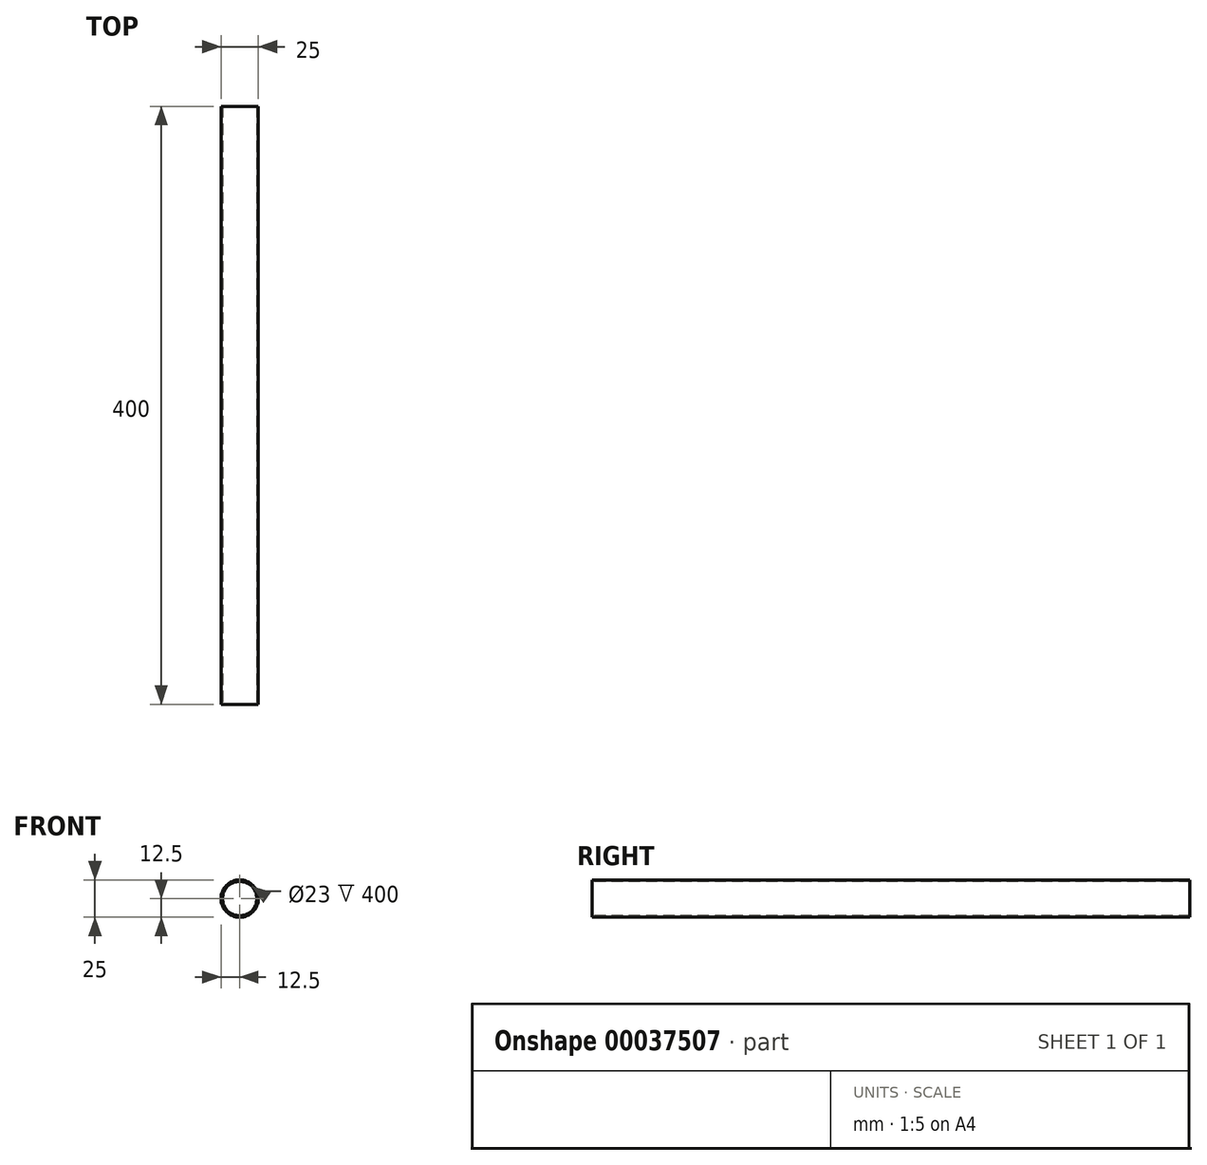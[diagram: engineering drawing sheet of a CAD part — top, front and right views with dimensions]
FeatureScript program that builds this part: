
annotation { "Feature Type Name" : "Feature", "Feature Type Description" : "" }
export const myFeature = defineFeature(function(context is Context, id is Id, definition is map)
    precondition{}
    {
        {
            var Q0;
            Q0=qCreatedBy(makeId("Front.planeOp"),FACE);
            var sketch = newSketch(context, id + "F0", { "sketchPlane" : qUnion([Q0])});
            skCircle(sketch, "E0", {"center": v(0, 0) * mm, "radius": 12.5 * mm});
            skSolve(sketch);
        }
        {
            var Q0;
            Q0=makeQuery(id+"F0.imprint","IMPRINT",FACE,{"disambiguationData":[TD([[makeQuery(id+"F0.imprint","IMPRINT",EDGE,{"derivedFrom":sQuery(id+"F0.wireOp",EDGE,"E0")}),1.0]])]});
            extrude(context, id + "F1", {"entities" : qUnion([Q0]), "endBound" : BoundingType.SYMMETRIC, "depth" : 400 * mm});
        }
        {
            var Q0;
            Q0=makeQuery(id+"F1.opExtrude","CAP_FACE",FACE,{"disambiguationData":[OSD([sQuery(id+"F0.wireOp",EDGE,"E0")])],"isStart":false});
            var sketch = newSketch(context, id + "F2", { "sketchPlane" : qUnion([Q0])});
            skCircle(sketch, "E1", {"center": v(0, 0) * mm, "radius": 10.5 * mm});
            skSolve(sketch);
        }
        {
            var Q0;
            Q0=sQuery(id+"F2.wireOp",VERTEX,"E1.center");
            var Q1;
            Q1=makeQuery(id+"F1.opExtrude","SWEPT_BODY",BODY,{"disambiguationData":[OSD([sQuery(id+"F0.wireOp",EDGE,"E0")])]});
            hole(context, id + "F3", {"style" : HoleStyle.SIMPLE, "holeDiameter" : 23 * mm, "endStyle" : HoleEndStyle.THROUGH, "locations" : qUnion([Q0]), "scope" : qUnion([Q1])});
        }
    });
